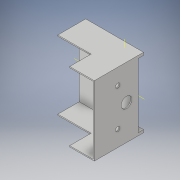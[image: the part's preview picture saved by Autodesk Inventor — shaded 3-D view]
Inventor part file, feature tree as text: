
AUTODESK INVENTOR PART (.ipt)
format: ipt  version: 2019.4 (Build 234330000, 330)  size: 162,304 bytes
history: native  units: mm
features: extrude x5, sketch x5, mirror x1
ambient origin geometry x8: Origin, YZ Plane, XZ Plane, XY Plane, X Axis, Y Axis, Z Axis, Center Point
bodies: Solid1 (feature_tree)
feature tree (11):
  extrude  "Extrusion1"  Depth=40.0mm TaperAngle=0.0deg
  extrude  "Extrusion2"  Depth=40.0mm TaperAngle=0.0deg
  extrude  "Extrusion3"  Depth=1.0mm
  extrude  "Extrusion4"  Depth=1.0mm
  mirror  "Mirror1"
  extrude  "Extrusion7"  Depth=5.0mm
  sketch  "Sketch1"  dims[d0=1.0mm d1=0.0mm d2=40.0mm d3=0.0mm]
  sketch  "Sketch2"  dims[d4=1.0mm d5=40.0mm d6=0.0mm]
  sketch  "Sketch3"  dims[d7=10.0mm d9=1.0mm]
  sketch  "Sketch4"  dims[d10=1.0mm d11=0.0mm d13=4.2mm]
  sketch  "Sketch7"  dims[d14=19.3mm d16=35.0mm d24=20.0mm d25=23.0mm d30=60.0mm d31=5.0mm d32=0.0mm]
